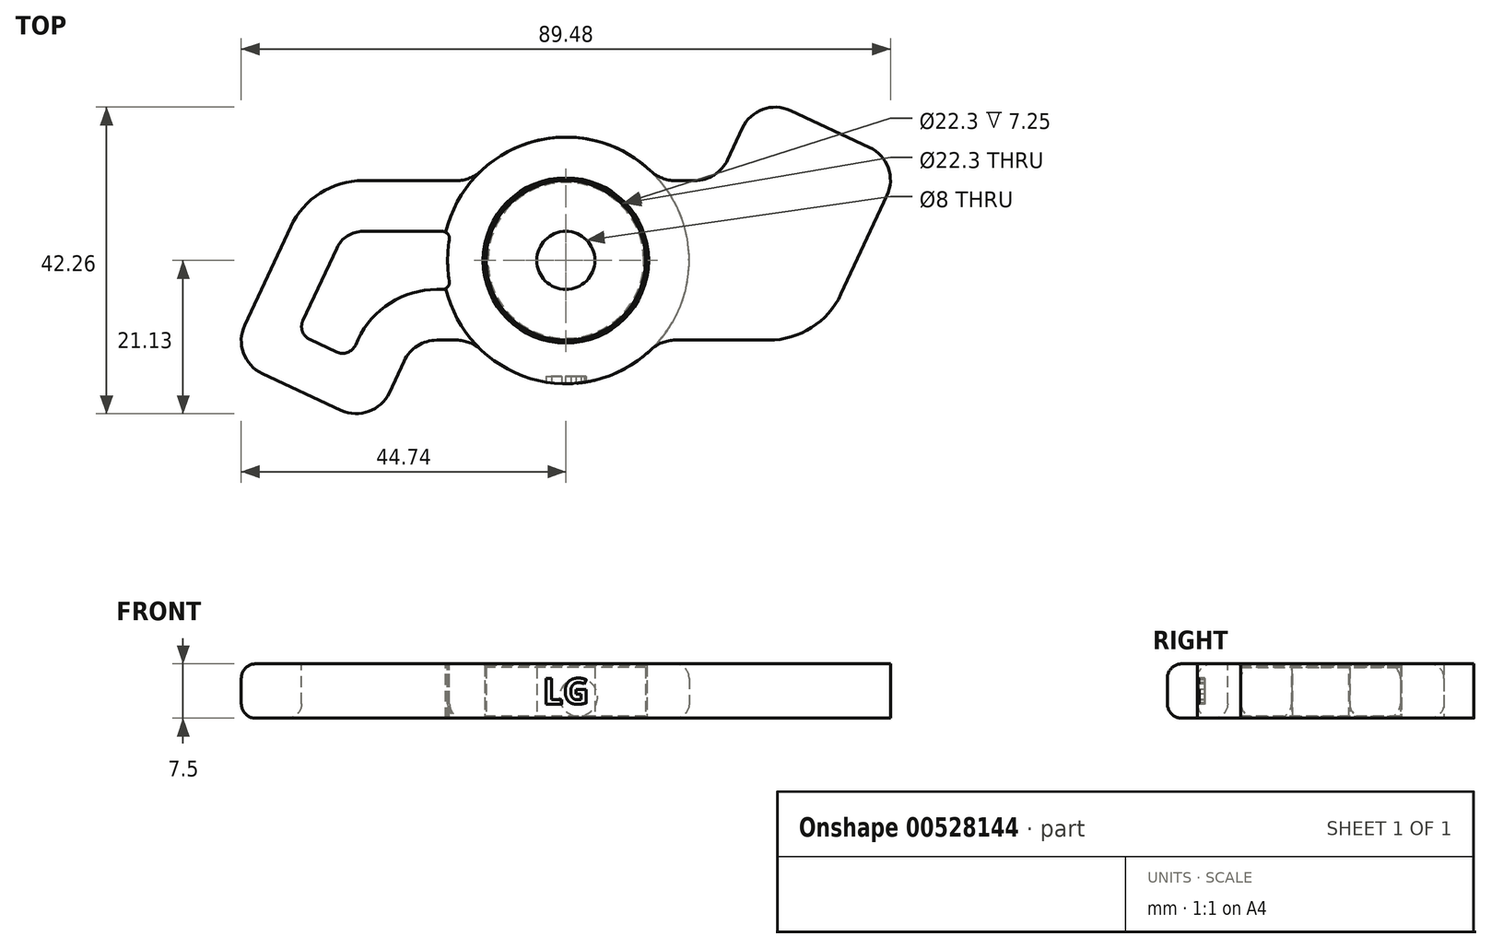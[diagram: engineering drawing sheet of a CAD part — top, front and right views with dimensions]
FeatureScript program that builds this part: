
annotation { "Feature Type Name" : "Feature", "Feature Type Description" : "" }
export const myFeature = defineFeature(function(context is Context, id is Id, definition is map)
    precondition{}
    {
        {
            var Q0;
            Q0=qCreatedBy(makeId("Top.planeOp"),FACE);
            var sketch = newSketch(context, id + "F0", { "sketchPlane" : qUnion([Q0])});
            skCircle(sketch, "E0", {"center": v(0, 0) * mm, "radius": 11 * mm});
            skCircle(sketch, "E1", {"center": v(0, 0) * mm, "radius": 4 * mm});
            skSolve(sketch);
        }
        {
            var Q0;
            Q0=makeQuery(id+"F0.imprint","IMPRINT",FACE,{"disambiguationData":[TD([[makeQuery(id+"F0.imprint","IMPRINT",EDGE,{"derivedFrom":sQuery(id+"F0.wireOp",EDGE,"E0")}),1.0]])]});
            extrude(context, id + "F1", {"entities" : qUnion([Q0]), "depth" : 7 * mm, "offsetDistance" : 25 * mm});
        }
        {
            var Q0;
            Q0=qCreatedBy(makeId("Top.planeOp"),FACE);
            var sketch = newSketch(context, id + "F2", { "sketchPlane" : qUnion([Q0])});
            skLineSegment(sketch, "E2.bottom", {"start": v(-27.96, 11) * mm, "end": v(-15.1, 11) * mm});
            skLineSegment(sketch, "E2.top", {"start": v(-17.77, -11) * mm, "end": v(-15.1, -11) * mm});
            skPoint(sketch, "E2.middle", {"position": v(0, 0) * mm});
            skArc(sketch, "E3.0", {"start": v(-11.67, -12.36) * mm, "mid": v(17, 0) * mm, "end": v(-11.67, 12.36) * mm});
            skPoint(sketch, "E2.right.start.orphan", {"position": v(27.96, 11) * mm});
            skPoint(sketch, "E4.orphan", {"position": v(27.96, -11) * mm});
            skArc(sketch, "E5", {"start": v(-27.96, 11) * mm, "mid": v(-33.87, 9.28) * mm, "end": v(-37.93, 4.65) * mm});
            skLineSegment(sketch, "E6.bottom", {"start": v(-41.85, -15.6) * mm, "end": v(-30.98, -20.66) * mm});
            skLineSegment(sketch, "E6.left", {"start": v(-44.27, -8.95) * mm, "end": v(-37.93, 4.65) * mm});
            skLineSegment(sketch, "E6.right", {"start": v(-24.33, -18.24) * mm, "end": v(-22.3, -13.89) * mm});
            skPoint(sketch, "E7.orphan", {"position": v(-27.96, -11) * mm});
            skPoint(sketch, "E8.visualSharp", {"position": v(-46.38, -13.48) * mm});
            skArc(sketch, "E8.filletArc", {"start": v(-44.27, -8.95) * mm, "mid": v(-44.44, -12.77) * mm, "end": v(-41.85, -15.6) * mm});
            skPoint(sketch, "E9.visualSharp", {"position": v(-26.44, -22.77) * mm});
            skArc(sketch, "E9.filletArc", {"start": v(-30.98, -20.66) * mm, "mid": v(-27.15, -20.83) * mm, "end": v(-24.33, -18.24) * mm});
            skPoint(sketch, "E10.visualSharp", {"position": v(-20.95, -11) * mm});
            skArc(sketch, "E10.filletArc", {"start": v(-17.77, -11) * mm, "mid": v(-20.45, -11.78) * mm, "end": v(-22.3, -13.89) * mm});
            skPoint(sketch, "E11.visualSharp", {"position": v(-12.96, -11) * mm});
            skArc(sketch, "E11.filletArc", {"start": v(-11.67, -12.36) * mm, "mid": v(-13.25, -11.35) * mm, "end": v(-15.1, -11) * mm});
            skPoint(sketch, "E12.visualSharp", {"position": v(-12.96, 11) * mm});
            skArc(sketch, "E12.filletArc", {"start": v(-15.1, 11) * mm, "mid": v(-13.25, 11.35) * mm, "end": v(-11.67, 12.36) * mm});
            skCircle(sketch, "E13.0", {"center": v(0, 0) * mm, "radius": 11.15 * mm});
            skSolve(sketch);
        }
        {
            var Q0;
            Q0=makeQuery(id+"F2.imprint","IMPRINT",FACE,{"disambiguationData":[TD([[makeQuery(id+"F2.imprint","IMPRINT",EDGE,{"derivedFrom":sQuery(id+"F2.wireOp",EDGE,"E2.bottom")}),-1.0]])]});
            extrude(context, id + "F3", {"entities" : qUnion([Q0]), "depth" : 7.5 * mm, "offsetDistance" : 25 * mm});
        }
        {
            var Q0;
            Q0=makeQuery(id+"F3.opExtrude","SWEPT_BODY",BODY,{"disambiguationData":[OSD([sQuery(id+"F2.wireOp",EDGE,"E2.bottom"),sQuery(id+"F2.wireOp",EDGE,"E2.top"),sQuery(id+"F2.wireOp",EDGE,"E3.0"),sQuery(id+"F2.wireOp",EDGE,"E5"),sQuery(id+"F2.wireOp",EDGE,"E6.bottom"),sQuery(id+"F2.wireOp",EDGE,"E6.left"),sQuery(id+"F2.wireOp",EDGE,"E6.right"),sQuery(id+"F2.wireOp",EDGE,"E8.filletArc"),sQuery(id+"F2.wireOp",EDGE,"E9.filletArc"),sQuery(id+"F2.wireOp",EDGE,"E10.filletArc"),sQuery(id+"F2.wireOp",EDGE,"E11.filletArc"),sQuery(id+"F2.wireOp",EDGE,"E12.filletArc"),sQuery(id+"F2.wireOp",EDGE,"E13.0")])]});
            var Q1;
            Q1=makeQuery(id+"F3.opExtrude","CAP_EDGE",EDGE,{"disambiguationData":[OSD([sQuery(id+"F2.wireOp",EDGE,"E13.0")])],"isStart":false});
            circularPattern(context, id + "F4", {"operationType" : NewBodyOperationType.ADD, "entities" : qUnion([Q0]), "axis" : qUnion([Q1]), "angle" : 360 * degree, "instanceCount" : 2, "equalSpace" : true});
        }
        {
            var Q0;
            Q0=makeQuery(id+"F3.opExtrude","CAP_FACE",FACE,{"disambiguationData":[OSD([sQuery(id+"F2.wireOp",EDGE,"E2.bottom"),sQuery(id+"F2.wireOp",EDGE,"E2.top"),sQuery(id+"F2.wireOp",EDGE,"E3.0"),sQuery(id+"F2.wireOp",EDGE,"E5"),sQuery(id+"F2.wireOp",EDGE,"E6.bottom"),sQuery(id+"F2.wireOp",EDGE,"E6.left"),sQuery(id+"F2.wireOp",EDGE,"E6.right"),sQuery(id+"F2.wireOp",EDGE,"E8.filletArc"),sQuery(id+"F2.wireOp",EDGE,"E9.filletArc"),sQuery(id+"F2.wireOp",EDGE,"E10.filletArc"),sQuery(id+"F2.wireOp",EDGE,"E11.filletArc"),sQuery(id+"F2.wireOp",EDGE,"E12.filletArc"),sQuery(id+"F2.wireOp",EDGE,"E13.0")])],"isStart":false});
            var sketch = newSketch(context, id + "F5", { "sketchPlane" : qUnion([Q0])});
            skLineSegment(sketch, "E14.0", {"start": v(-27.96, 4) * mm, "end": v(-17.04, 4) * mm});
            skArc(sketch, "E14.1", {"start": v(-27.96, 4) * mm, "mid": v(-30.11, 3.37) * mm, "end": v(-31.59, 1.7) * mm});
            skLineSegment(sketch, "E14.2", {"start": v(-36.24, -8.28) * mm, "end": v(-31.59, 1.7) * mm});
            skLineSegment(sketch, "E14.3", {"start": v(-17.77, -4) * mm, "end": v(-17.04, -4) * mm});
            skArc(sketch, "E14.4", {"start": v(-17.77, -4) * mm, "mid": v(-24.22, -5.88) * mm, "end": v(-28.64, -10.93) * mm});
            skLineSegment(sketch, "E14.5", {"start": v(-28.99, -11.66) * mm, "end": v(-28.64, -10.93) * mm});
            skLineSegment(sketch, "E14.6", {"start": v(-35.27, -10.94) * mm, "end": v(-31.64, -12.63) * mm});
            skPoint(sketch, "E15.visualSharp", {"position": v(-37.08, -10.1) * mm});
            skArc(sketch, "E15.filletArc", {"start": v(-36.24, -8.28) * mm, "mid": v(-36.3, -9.8) * mm, "end": v(-35.27, -10.94) * mm});
            skPoint(sketch, "E16.visualSharp", {"position": v(-29.83, -13.47) * mm});
            skArc(sketch, "E16.filletArc", {"start": v(-31.64, -12.63) * mm, "mid": v(-30.11, -12.7) * mm, "end": v(-28.99, -11.66) * mm});
            skArc(sketch, "E17.0", {"start": v(-16.05, 2.83) * mm, "mid": v(-16.3, 0) * mm, "end": v(-16.05, -2.83) * mm});
            skPoint(sketch, "E18.visualSharp", {"position": v(-15.8, 4) * mm});
            skArc(sketch, "E18.filletArc", {"start": v(-16.05, 2.83) * mm, "mid": v(-16.27, 3.64) * mm, "end": v(-17.04, 4) * mm});
            skPoint(sketch, "E19.visualSharp", {"position": v(-15.8, -4) * mm});
            skArc(sketch, "E19.filletArc", {"start": v(-17.04, -4) * mm, "mid": v(-16.27, -3.64) * mm, "end": v(-16.05, -2.83) * mm});
            skSolve(sketch);
        }
        {
            var Q0;
            Q0=makeQuery(id+"F5.imprint","IMPRINT",FACE,{"disambiguationData":[TD([[makeQuery(id+"F5.imprint","IMPRINT",EDGE,{"derivedFrom":sQuery(id+"F5.wireOp",EDGE,"E14.0")}),-1.0]])]});
            extrude(context, id + "F6", {"entities" : qUnion([Q0]), "operationType" : NewBodyOperationType.REMOVE, "oppositeDirection" : true, "depth" : 25 * mm, "offsetDistance" : 25 * mm});
        }
        {
            var Q0;
            Q0=makeQuery(id+"F6.boolean.opBoolean","COPY",EDGE,{"derivedFrom":makeQuery(id+"F6.opExtrude","CAP_EDGE",EDGE,{"disambiguationData":[OSD([sQuery(id+"F5.wireOp",EDGE,"E14.0")])],"isStart":true})});
            var Q1;
            {var subQ0=makeQuery(id+"F3.opExtrude","CAP_FACE",FACE,{"disambiguationData":[OSD([sQuery(id+"F2.wireOp",EDGE,"E2.bottom"),sQuery(id+"F2.wireOp",EDGE,"E2.top"),sQuery(id+"F2.wireOp",EDGE,"E3.0"),sQuery(id+"F2.wireOp",EDGE,"E5"),sQuery(id+"F2.wireOp",EDGE,"E6.bottom"),sQuery(id+"F2.wireOp",EDGE,"E6.left"),sQuery(id+"F2.wireOp",EDGE,"E6.right"),sQuery(id+"F2.wireOp",EDGE,"E8.filletArc"),sQuery(id+"F2.wireOp",EDGE,"E9.filletArc"),sQuery(id+"F2.wireOp",EDGE,"E10.filletArc"),sQuery(id+"F2.wireOp",EDGE,"E11.filletArc"),sQuery(id+"F2.wireOp",EDGE,"E12.filletArc"),sQuery(id+"F2.wireOp",EDGE,"E13.0")])],"isStart":true});Q1=makeQuery(id+"F6.boolean.opBoolean","INTERSECT",EDGE,{"derivedFrom":[makeQuery(id+"F4.boolean.opBoolean","MERGE",FACE,{"derivedFrom":[subQ0,makeQuery(id+"F4.opPattern","COPY",FACE,{"derivedFrom":subQ0,"instanceName":"1"})]}),makeQuery(id+"F6.opExtrude","SWEPT_FACE",FACE,{"disambiguationData":[OSD([sQuery(id+"F5.wireOp",EDGE,"E14.6")])]})]});}
            fillet(context, id + "F7", {"entities" : qUnion([Q0, Q1]), "radius" : 2 * mm, "tangentPropagation" : true, "allowEdgeOverflow" : false});
        }
        {
            var Q0;
            {var subQ0=sQuery(id+"F2.wireOp",EDGE,"E12.filletArc");var subQ2=sQuery(id+"F2.wireOp",EDGE,"E3.0");Q0=makeQuery(id+"F4.boolean.opBoolean","SPLIT",EDGE,{"disambiguationData":[TD([makeQuery(id+"F3.opExtrude","SWEPT_FACE",FACE,{"disambiguationData":[OSD([subQ0])]})])],"derivedFrom":makeQuery(id+"F3.opExtrude","CAP_EDGE",EDGE,{"disambiguationData":[OSD([subQ2])],"isStart":true})});}
            var Q1;
            {var subQ0=sQuery(id+"F2.wireOp",EDGE,"E12.filletArc");var subQ2=sQuery(id+"F2.wireOp",EDGE,"E3.0");Q1=makeQuery(id+"F4.boolean.opBoolean","SPLIT",EDGE,{"disambiguationData":[TD([makeQuery(id+"F3.opExtrude","SWEPT_FACE",FACE,{"disambiguationData":[OSD([subQ0])]})])],"derivedFrom":makeQuery(id+"F3.opExtrude","CAP_EDGE",EDGE,{"disambiguationData":[OSD([subQ2])],"isStart":false})});}
            fillet(context, id + "F8", {"entities" : qUnion([Q0, Q1]), "radius" : 2 * mm, "tangentPropagation" : true, "allowEdgeOverflow" : false});
        }
        {
            var Q0;
            Q0=makeQuery(id+"F3.opExtrude","CAP_EDGE",EDGE,{"disambiguationData":[OSD([sQuery(id+"F2.wireOp",EDGE,"E13.0")])],"isStart":false});
            var Q1;
            Q1=makeQuery(id+"F1.opExtrude","CAP_EDGE",EDGE,{"disambiguationData":[OSD([sQuery(id+"F0.wireOp",EDGE,"E0")])],"isStart":true});
            chamfer(context, id + "F9", {"entities" : qUnion([Q0, Q1]), "width" : .25 * mm, "tangentPropagation" : true});
        }
        {
            var Q0;
            Q0=qCreatedBy(makeId("Front.planeOp"),FACE);
            cPlane(context, id + "F10", {"entities" : qUnion([Q0]), "cplaneType" : CPlaneType.OFFSET, "offset" : 25 * mm, "width" : 150 * mm, "height" : 150 * mm});
        }
        {
            var Q0;
            Q0=qCreatedBy(id+"F10.planeOp",FACE);
            var sketch = newSketch(context, id + "F11", { "sketchPlane" : qUnion([Q0])});
            skText(sketch, "E20", { "text": "LG", "fontName": "OpenSans-Bold.ttf"});
            const initialGuessF11  = {"E20": [-0.00317, 0.00196, 1, 0, 0.00356]};
            skSetInitialGuess(sketch, initialGuessF11);
            skSolve(sketch);
        }
        {
            var Q0;
            Q0 = qSketchRegion(id + "F11", true);
            extrude(context, id + "F12", {"entities" : qUnion([Q0]), "operationType" : NewBodyOperationType.REMOVE, "oppositeDirection" : true, "depth" : 9 * mm, "offsetDistance" : 25 * mm});
        }
    });
